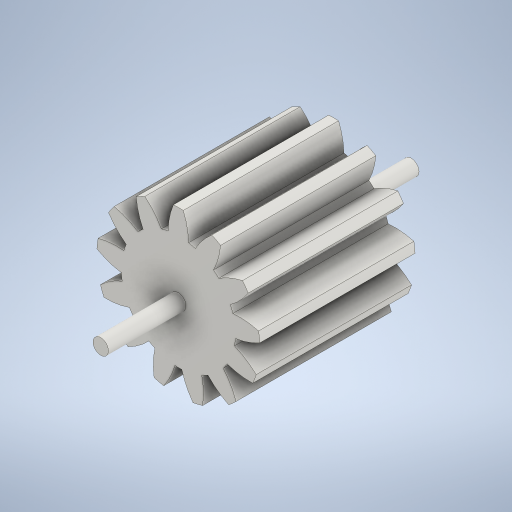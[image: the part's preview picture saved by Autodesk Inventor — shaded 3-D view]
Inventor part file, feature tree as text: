
AUTODESK INVENTOR PART (.ipt)
format: ipt  version: 2023.2 (Build 272271000, 271)  size: 404,480 bytes
history: native  units: mm (DEFAULTED — no unit token found)
features: plane x3, other x3, sketch x3, extrude x2
ambient origin geometry x8: Origin, YZ Plane, XZ Plane, XY Plane, X Axis, Y Axis, Z Axis, Center Point
bodies: Solid1 (feature_tree)
feature tree (11):
  extrude  "Extrusion1"  Depth=10.0mm TaperAngle=0.0deg
  plane  "Work Plane2"
  plane  "Work Plane8"
  plane  "Work Plane9"
  other  "Spur Gear"
  extrude  "Extrusion2"  Depth=10.0mm TaperAngle=0.0deg
  sketch  "Sketch1"  dims[d0=10.503525mm d1=10.0mm d2=0.0mm]
  sketch  "Sketch2"  dims[d3=9.1mm d4=10.0mm d5=0.0mm]
  other  "Srf1"
  sketch  "Sketch3"  dims[d16=12.604893mm d17=0.0mm d34=2.41661mm d39=0.0mm d41=0.0mm d43=12.604893mm d46=12.604893mm d47=0.0mm d48=0.0mm d49=1.0mm d50=5.0mm d51=15.0mm d52=0.0mm d53=0.0mm]
  other  "Pitch Diameter"
